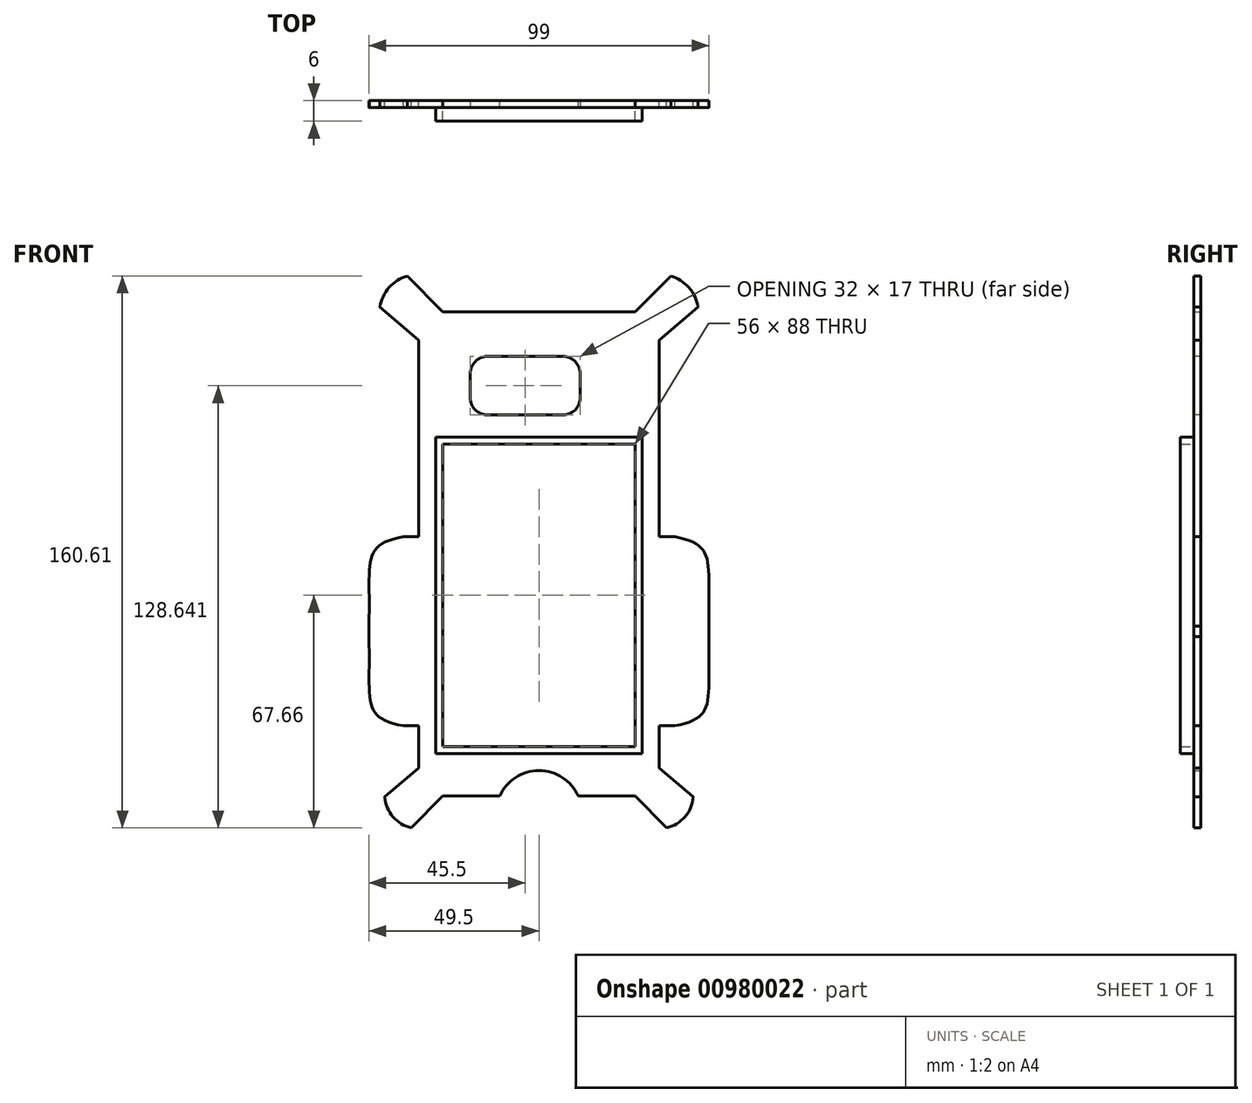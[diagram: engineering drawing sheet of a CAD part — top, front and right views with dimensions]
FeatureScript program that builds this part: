
annotation { "Feature Type Name" : "Feature", "Feature Type Description" : "" }
export const myFeature = defineFeature(function(context is Context, id is Id, definition is map)
    precondition{}
    {
        {
            var Q0;
            Q0=qCreatedBy(makeId("Front.planeOp"),FACE);
            var sketch = newSketch(context, id + "F0", { "sketchPlane" : qUnion([Q0])});
            skPoint(sketch, "E0.middle", {"position": v(0, 0) * mm});
            skLineSegment(sketch, "E1", {"start": v(35, 62.2) * mm, "end": v(35, 5) * mm});
            skLineSegment(sketch, "E2", {"start": v(-35, -62.2) * mm, "end": v(-35, -50) * mm});
            skLineSegment(sketch, "E3", {"start": v(0, 0) * mm, "end": v(0, 70) * mm, "construction": true});
            skLineSegment(sketch, "E4", {"start": v(0, 0) * mm, "end": v(0, -70) * mm, "construction": true});
            skLineSegment(sketch, "E5", {"start": v(27.98, 70.44) * mm, "end": v(-27.98, 70.44) * mm});
            skLineSegment(sketch, "E6", {"start": v(27.98, -70.44) * mm, "end": v(11.42, -70.44) * mm});
            skFitSpline(sketch, "E7", {"points": [v(39.5, 5) * mm, v(49.5, -20.96) * mm], "startDerivative": vector(38.05, -7.02) * mm, "endDerivative": vector(2.03, -55.33) * mm});
            skLineSegment(sketch, "E8", {"start": v(27.9, -22.5) * mm, "end": v(67.22, -22.5) * mm, "construction": true});
            skFitSpline(sketch, "E9.MirrorCS", {"points": [v(39.5, -50) * mm, v(49.5, -24.04) * mm], "startDerivative": vector(38.05, 7.02) * mm, "endDerivative": vector(2.03, 55.33) * mm});
            skLineSegment(sketch, "E10", {"start": v(49.5, -20.96) * mm, "end": v(49.5, -24.04) * mm});
            skLineSegment(sketch, "E11.trimOffspring", {"start": v(35, -50) * mm, "end": v(35, -62.2) * mm});
            skLineSegment(sketch, "E12", {"start": v(39.5, 5) * mm, "end": v(35, 5) * mm});
            skLineSegment(sketch, "E13", {"start": v(39.5, -50) * mm, "end": v(35, -50) * mm});
            skFitSpline(sketch, "E14.MirrorCS", {"points": [v(-39.5, 5) * mm, v(-49.5, -20.96) * mm], "startDerivative": vector(-38.05, -7.02) * mm, "endDerivative": vector(-2.03, -55.33) * mm});
            skFitSpline(sketch, "E15.MirrorCS", {"points": [v(-39.5, -50) * mm, v(-49.5, -24.04) * mm], "startDerivative": vector(-38.05, 7.02) * mm, "endDerivative": vector(-2.03, 55.33) * mm});
            skLineSegment(sketch, "E16.MirrorCS", {"start": v(-39.5, 5) * mm, "end": v(-35, 5) * mm});
            skLineSegment(sketch, "E17.MirrorCS", {"start": v(-39.5, -50) * mm, "end": v(-35, -50) * mm});
            skLineSegment(sketch, "E18.trimOffspring", {"start": v(-35, 5) * mm, "end": v(-35, 62.2) * mm});
            skLineSegment(sketch, "E19", {"start": v(-67.17, 0) * mm, "end": v(113.75, 0) * mm, "construction": true});
            skLineSegment(sketch, "E20", {"start": v(35, 62.2) * mm, "end": v(46.28, 71.82) * mm});
            skLineSegment(sketch, "E21", {"start": v(27.98, 70.44) * mm, "end": v(38.36, 80.93) * mm});
            skArc(sketch, "E22", {"start": v(38.36, 80.93) * mm, "mid": v(43.62, 77.5) * mm, "end": v(46.28, 71.82) * mm});
            skLineSegment(sketch, "E23.MirrorCS", {"start": v(-27.98, 70.44) * mm, "end": v(-38.36, 80.93) * mm});
            skArc(sketch, "E24.MirrorCS", {"start": v(-38.36, 80.93) * mm, "mid": v(-43.62, 77.5) * mm, "end": v(-46.28, 71.82) * mm});
            skLineSegment(sketch, "E25.MirrorCS", {"start": v(-35, 62.2) * mm, "end": v(-46.28, 71.82) * mm});
            skLineSegment(sketch, "E26", {"start": v(-49.5, -20.96) * mm, "end": v(-49.5, -24.04) * mm});
            skArc(sketch, "E27", {"start": v(-11.42, -70.44) * mm, "mid": v(0, -62.99) * mm, "end": v(11.42, -70.44) * mm});
            skLineSegment(sketch, "E28.trimOffspring", {"start": v(-11.42, -70.44) * mm, "end": v(-27.98, -70.44) * mm});
            skLineSegment(sketch, "E29", {"start": v(27.98, -70.44) * mm, "end": v(37.12, -79.68) * mm});
            skLineSegment(sketch, "E30", {"start": v(35, -62.2) * mm, "end": v(44.9, -70.64) * mm});
            skArc(sketch, "E31", {"start": v(44.9, -70.64) * mm, "mid": v(42.5, -76.44) * mm, "end": v(37.12, -79.68) * mm});
            skLineSegment(sketch, "E32.MirrorCS", {"start": v(-35, -62.2) * mm, "end": v(-44.9, -70.64) * mm});
            skLineSegment(sketch, "E33.MirrorCS", {"start": v(-27.98, -70.44) * mm, "end": v(-37.12, -79.68) * mm});
            skArc(sketch, "E34.MirrorCS", {"start": v(-44.9, -70.64) * mm, "mid": v(-42.5, -76.44) * mm, "end": v(-37.12, -79.68) * mm});
            skSolve(sketch);
        }
        {
            var Q0;
            Q0=qSketchRegion(id+"F0",true);
            extrude(context, id + "F1", {"entities" : qUnion([Q0]), "depth" : 2 * mm, "offsetDistance" : 25 * mm});
        }
        {
            var Q0;
            Q0=qCreatedBy(makeId("Front.planeOp"),FACE);
            var Q1;
            Q1=qBodyType(qCreatedBy(id+"F3",EDGE),BodyType.WIRE);
            cPlane(context, id + "F2", {"entities" : qUnion([Q0, Q1]), "cplaneType" : CPlaneType.OFFSET, "offset" : 2 * mm, "width" : 150 * mm, "height" : 150 * mm});
        }
        {
            var Q0;
            Q0=qCreatedBy(id+"F2.planeOp",FACE);
            var sketch = newSketch(context, id + "F3", { "sketchPlane" : qUnion([Q0])});
            skArc(sketch, "E35.MirrorCS", {"start": v(7, 57.46) * mm, "mid": v(10.54, 56) * mm, "end": v(12, 52.46) * mm});
            skArc(sketch, "E36.MirrorCS", {"start": v(-20, 52.46) * mm, "mid": v(-18.54, 56) * mm, "end": v(-15, 57.46) * mm});
            skArc(sketch, "E37.MirrorCS", {"start": v(-15, 40.46) * mm, "mid": v(-18.54, 41.93) * mm, "end": v(-20, 45.46) * mm});
            skArc(sketch, "E38.MirrorCS", {"start": v(12, 45.46) * mm, "mid": v(10.54, 41.93) * mm, "end": v(7, 40.46) * mm});
            skLineSegment(sketch, "E39.MirrorCS", {"start": v(-15, 57.46) * mm, "end": v(7, 57.46) * mm});
            skLineSegment(sketch, "E40.MirrorCS", {"start": v(12, 52.46) * mm, "end": v(12, 45.46) * mm});
            skLineSegment(sketch, "E41.MirrorCS", {"start": v(-20, 52.46) * mm, "end": v(-20, 45.46) * mm});
            skLineSegment(sketch, "E42.MirrorCS", {"start": v(-15, 40.46) * mm, "end": v(7, 40.46) * mm});
            skSolve(sketch);
        }
        {
            var Q0;
            Q0=qSketchRegion(id+"F3",true);
            extrude(context, id + "F4", {"entities" : qUnion([Q0]), "operationType" : NewBodyOperationType.REMOVE, "oppositeDirection" : true, "depth" : 3 * mm, "offsetDistance" : 25 * mm});
        }
        {
            var Q0;
            Q0=qCreatedBy(id+"F2.planeOp",FACE);
            var sketch = newSketch(context, id + "F5", { "sketchPlane" : qUnion([Q0])});
            skPoint(sketch, "E43.middle", {"position": v(0, 0) * mm});
            skLineSegment(sketch, "E44.left", {"start": v(-28, 31.98) * mm, "end": v(-28, -56.02) * mm});
            skLineSegment(sketch, "E44.right", {"start": v(28, 31.98) * mm, "end": v(28, -56.02) * mm});
            skPoint(sketch, "E44.middle", {"position": v(0, -12.02) * mm});
            skLineSegment(sketch, "E45.left", {"start": v(-30, 33.98) * mm, "end": v(-30, -58.02) * mm});
            skLineSegment(sketch, "E45.right", {"start": v(30, 33.98) * mm, "end": v(30, -58.02) * mm});
            skLineSegment(sketch, "E46", {"start": v(28, -56.02) * mm, "end": v(-8.7, -56.02) * mm});
            skLineSegment(sketch, "E47", {"start": v(-8.7, -58.02) * mm, "end": v(30, -58.02) * mm});
            skLineSegment(sketch, "E48", {"start": v(-28, -56.02) * mm, "end": v(-8.7, -56.02) * mm});
            skLineSegment(sketch, "E49", {"start": v(-8.7, -58.02) * mm, "end": v(-30, -58.02) * mm});
            skLineSegment(sketch, "E50", {"start": v(28, 31.98) * mm, "end": v(-8.7, 31.98) * mm});
            skLineSegment(sketch, "E51", {"start": v(-8.7, 33.98) * mm, "end": v(30, 33.98) * mm});
            skLineSegment(sketch, "E52", {"start": v(-30, 33.98) * mm, "end": v(-8.7, 33.98) * mm});
            skLineSegment(sketch, "E53", {"start": v(-8.7, 31.98) * mm, "end": v(-28, 31.98) * mm});
            skPoint(sketch, "E54.orphan", {"position": v(-29.35, 33.98) * mm});
            skSolve(sketch);
        }
        {
            var Q0;
            Q0=makeQuery(id+"F5.imprint","IMPRINT",FACE,{"disambiguationData":[TD([[makeQuery(id+"F5.imprint","IMPRINT",EDGE,{"derivedFrom":sQuery(id+"F5.wireOp",EDGE,"E44.bottom")}),1.0]])]});
            var Q1;
            Q1=makeQuery(id+"F5.imprint","IMPRINT",FACE,{"disambiguationData":[TD([[makeQuery(id+"F5.imprint","IMPRINT",EDGE,{"derivedFrom":sQuery(id+"F5.wireOp",EDGE,"E44.right")}),1.0]])]});
            var Q2;
            Q2=makeQuery(id+"F5.imprint","IMPRINT",FACE,{"disambiguationData":[TD([[makeQuery(id+"F5.imprint","IMPRINT",EDGE,{"derivedFrom":sQuery(id+"F5.wireOp",EDGE,"E44.left")}),-1.0]])]});
            extrude(context, id + "F6", {"entities" : qUnion([Q0, Q1, Q2]), "depth" : 4 * mm, "offsetDistance" : 25 * mm});
        }
    });
